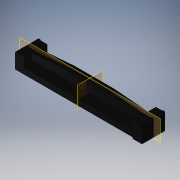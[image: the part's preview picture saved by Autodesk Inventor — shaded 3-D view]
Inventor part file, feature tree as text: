
AUTODESK INVENTOR PART (.ipt)
format: ipt  version: 2019 (Build 230136000, 136)  size: 228,864 bytes
history: native  units: mm (DEFAULTED — no unit token found)
features: other x16, sketch x8, extrude x5, fillet x1, pattern_linear x1
ambient origin geometry x8: Origin, YZ Plane, XZ Plane, XY Plane, X Axis, Y Axis, Z Axis, Center Point
bodies: Solid1 (feature_tree)
feature tree (31):
  extrude  "Extrusion1"  Depth=10.0mm
  extrude  "Extrusion2"  Depth=47.0mm
  extrude  "Extrusion3"  Depth=7.4676mm TaperAngle=0.0deg
  extrude  "Extrusion4"  Depth=2.54mm
  extrude  "Extrusion5"  Depth=1.3208mm
  fillet  "Fillet1"  Radius=0.762mm
  sketch  "Sketch8"  dims[d15=8.128mm]
  sketch  "Sketch9"  dims[d16=16.891mm]
  sketch  "Sketch11"  dims[d17=0.508mm d18=3.302mm d19=0.0mm d20=1.143mm d21=3.302mm d22=0.0mm d23=0.5842mm d37=0.508mm d38=0.5842mm d39=0.254mm d40=160.0mm d42=1.27mm d43=10.0mm d45=25.4mm d48=1.27mm d49=1.27mm d50=1.27mm d51=1.27mm d53=1.27mm d54=1.27mm d55=1.27mm d56=1.27mm d57=1.27mm d58=1.27mm d59=1.27mm d60=1.27mm d61=1.27mm d62=1.27mm d63=1.27mm d64=0.4318mm d65=2.032mm d66=20.0mm d68=22.86mm]
  pattern_linear  "Rectangular Pattern1"  Spacing1=3.302mm  [1 undecoded]
  sketch  "Sketch1"  dims[d0=55.0mm d1=10.0mm]
  sketch  "Sketch2"  dims[d2=7.4676mm d3=0.0mm d4=47.0mm]
  sketch  "Sketch3"  dims[d5=0.5842mm d6=7.4676mm d7=0.0mm]
  sketch  "Sketch4"  dims[d8=47.0mm d9=2.54mm]
  sketch  "Sketch5"  dims[d11=7.4676mm d12=0.0mm d13=1.3208mm d14=0.762mm]
  other  "Work Point66"
  other  "Work Point67"
  other  "Work Point68"
  other  "Work Point69"
  other  "Work Point70"
  other  "Work Point71"
  other  "Work Point72"
  other  "Work Point73"
  other  "Work Point74"
  other  "Work Point75"
  other  "Work Point76"
  other  "Work Point77"
  other  "Work Point78"
  other  "Work Point79"
  other  "Work Point80"
  other  "Work Point81"
note: 1 required parameter value undecoded (feature->parameter linkage not recoverable at this tier; creation-order binding heuristic only, values carry confidence <= 0.55)
